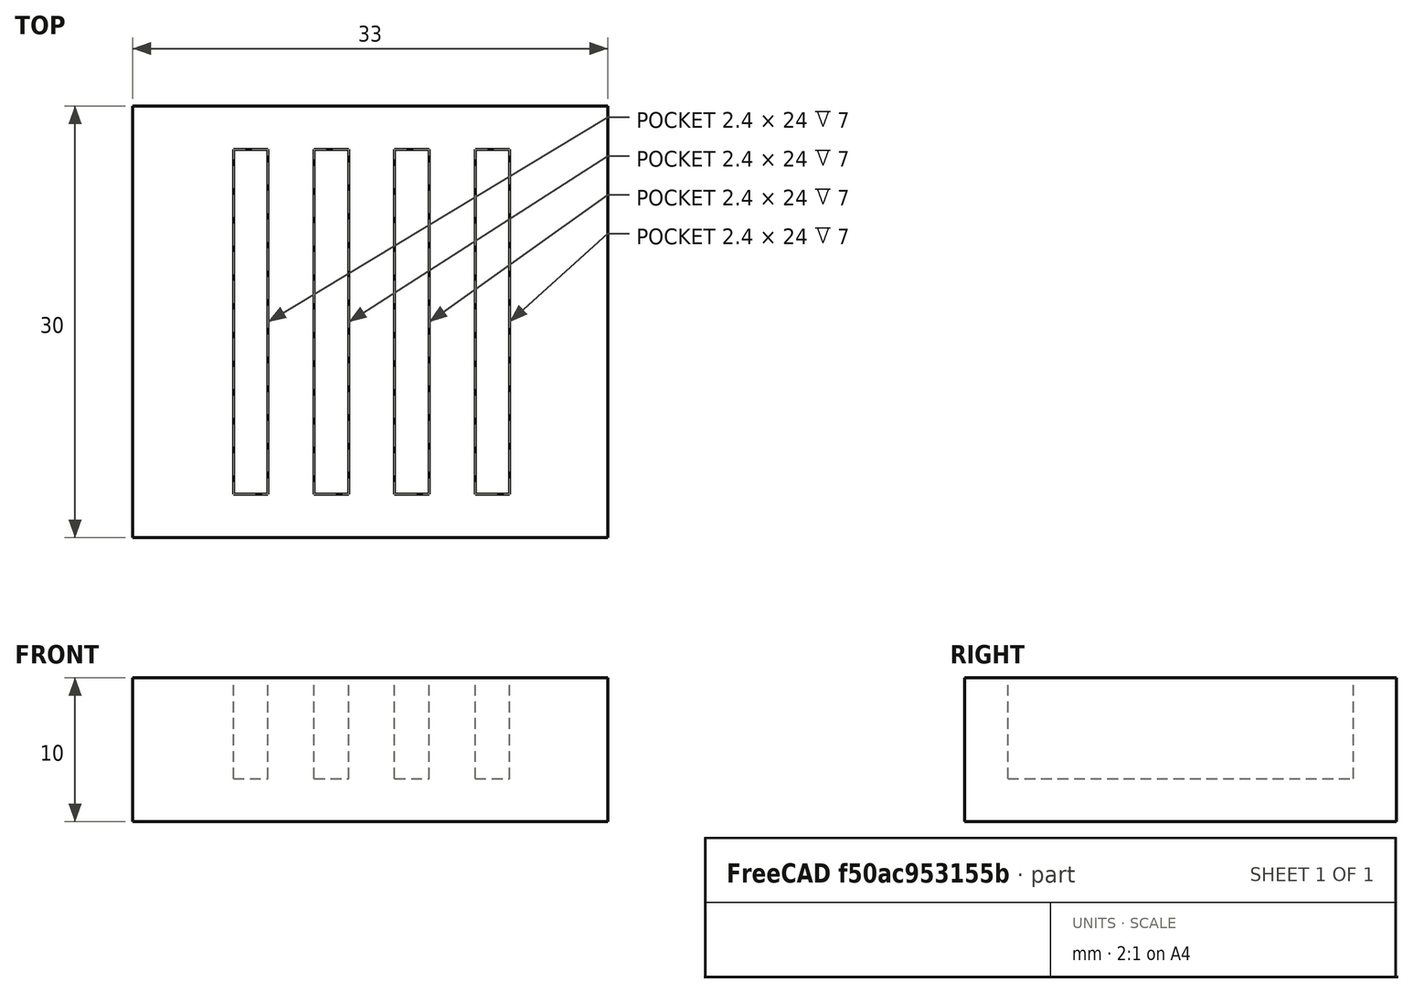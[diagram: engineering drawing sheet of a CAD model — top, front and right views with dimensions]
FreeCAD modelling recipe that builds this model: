
FCSTD DOCUMENT  (FreeCAD 0.21R33694 (Git))
Label: OJT1_T08R01_portatarjetitas
License: All rights reserved
LicenseURL: http://en.wikipedia.org/wiki/All_rights_reserved
objects: Part::Box×5, Part::MultiFuse×1, Part::Cut×1
note: 7 computed .brp shape members not serialized (recipe doc carries the construction recipe); baked Part::Feature solids carry a one-line shape summary decoded from their .brp

FEATURE [Part::Box] Box  label="Cube"
  AttacherType = Attacher::AttachEngine3D
  Height = 22
  Length = 2.4
  Placement = pos=(2.5,3,0) rot=(0,0,1;0rad)
  Width = 24
FEATURE [Part::Box] Box001  label="Cube001"
  AttacherType = Attacher::AttachEngine3D
  Height = 22
  Length = 2.4
  Placement = pos=(8.1,3,0) rot=(0,0,1;0rad)
  Width = 24
FEATURE [Part::Box] Box002  label="Cube002"
  AttacherType = Attacher::AttachEngine3D
  Height = 22
  Length = 2.4
  Placement = pos=(13.7,3,0) rot=(0,0,1;0rad)
  Width = 24
FEATURE [Part::Box] Box003  label="Cube003"
  AttacherType = Attacher::AttachEngine3D
  Height = 22
  Length = 2.4
  Placement = pos=(19.3,3,0) rot=(0,0,1;0rad)
  Width = 24
FEATURE [Part::MultiFuse] Fusion
  Placement = pos=(0,0,3) rot=(0,0,1;0rad)
  Refine = true
  Shapes = -> [Box,Box001,Box002,Box003]
FEATURE [Part::Box] Box004  label="Cube004"
  AttacherType = Attacher::AttachEngine3D
  Height = 10
  Length = 33
  Placement = pos=(-4.5,0,0) rot=(0,0,1;0rad)
  Width = 30
FEATURE [Part::Cut] Cut
  Base = -> Box004
  Refine = true
  Tool = -> Fusion
